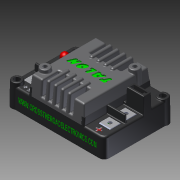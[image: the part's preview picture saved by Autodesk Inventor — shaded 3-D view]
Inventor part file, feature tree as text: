
AUTODESK INVENTOR PART (.ipt)
format: ipt  version: 2015 SP1 (Build 190203100, 203)  size: 4,917,760 bytes
history: native  units: in
note: dims shown in document units (in); Inventor stores cm internally (conversion verified against a paired STEP export)
features: other x19, imported_body x18, plane x1, sketch x1
ambient origin geometry x8: Origin, YZ Plane, XZ Plane, XY Plane, X Axis, Y Axis, Z Axis, Center Point
bodies: Body1 (feature_tree), Body2 (feature_tree), Body3 (feature_tree), Body4 (feature_tree), Body5 (feature_tree), Body6 (feature_tree), Body7 (feature_tree), Body8 (feature_tree), Body9 (feature_tree), Body10 (feature_tree), Body11 (feature_tree), Body12 (feature_tree), Body13 (feature_tree), Body14 (feature_tree), Body15 (feature_tree), Body16 (feature_tree), Body17 (feature_tree), Body18 (feature_tree)
feature tree (39):
  parser-record x1  (decoder bookkeeping rows leaked as tree rows — omitted from the tree; the rows remain in map.json)
  other  "Talon1"
  plane  "Work Plane1"
  sketch  "Sketch1"  dims[d0=90.0deg d1=2.446in d2=1.646in]
  other  "NONE_1"
  other  "NONE_2"
  other  "NONE_3"
  other  "NONE_4"
  other  "NONE_5"
  other  "NONE_6"
  other  "NONE_7"
  other  "NONE_8"
  other  "NONE_9"
  other  "NONE_10"
  other  "NONE_11"
  other  "NONE_12"
  other  "NONE_13"
  other  "NONE_14"
  other  "NONE_15"
  other  "NONE_16"
  other  "NONE_17"
  imported_body  "Base1"
  imported_body  "Base2"
  imported_body  "Base3"
  imported_body  "Base4"
  imported_body  "Base5"
  imported_body  "Base6"
  imported_body  "Base7"
  imported_body  "Base8"
  imported_body  "Base9"
  imported_body  "Base10"
  imported_body  "Base11"
  imported_body  "Base12"
  imported_body  "Base13"
  imported_body  "Base14"
  imported_body  "Base15"
  imported_body  "Base16"
  imported_body  "Base17"
  imported_body  "Base18"
